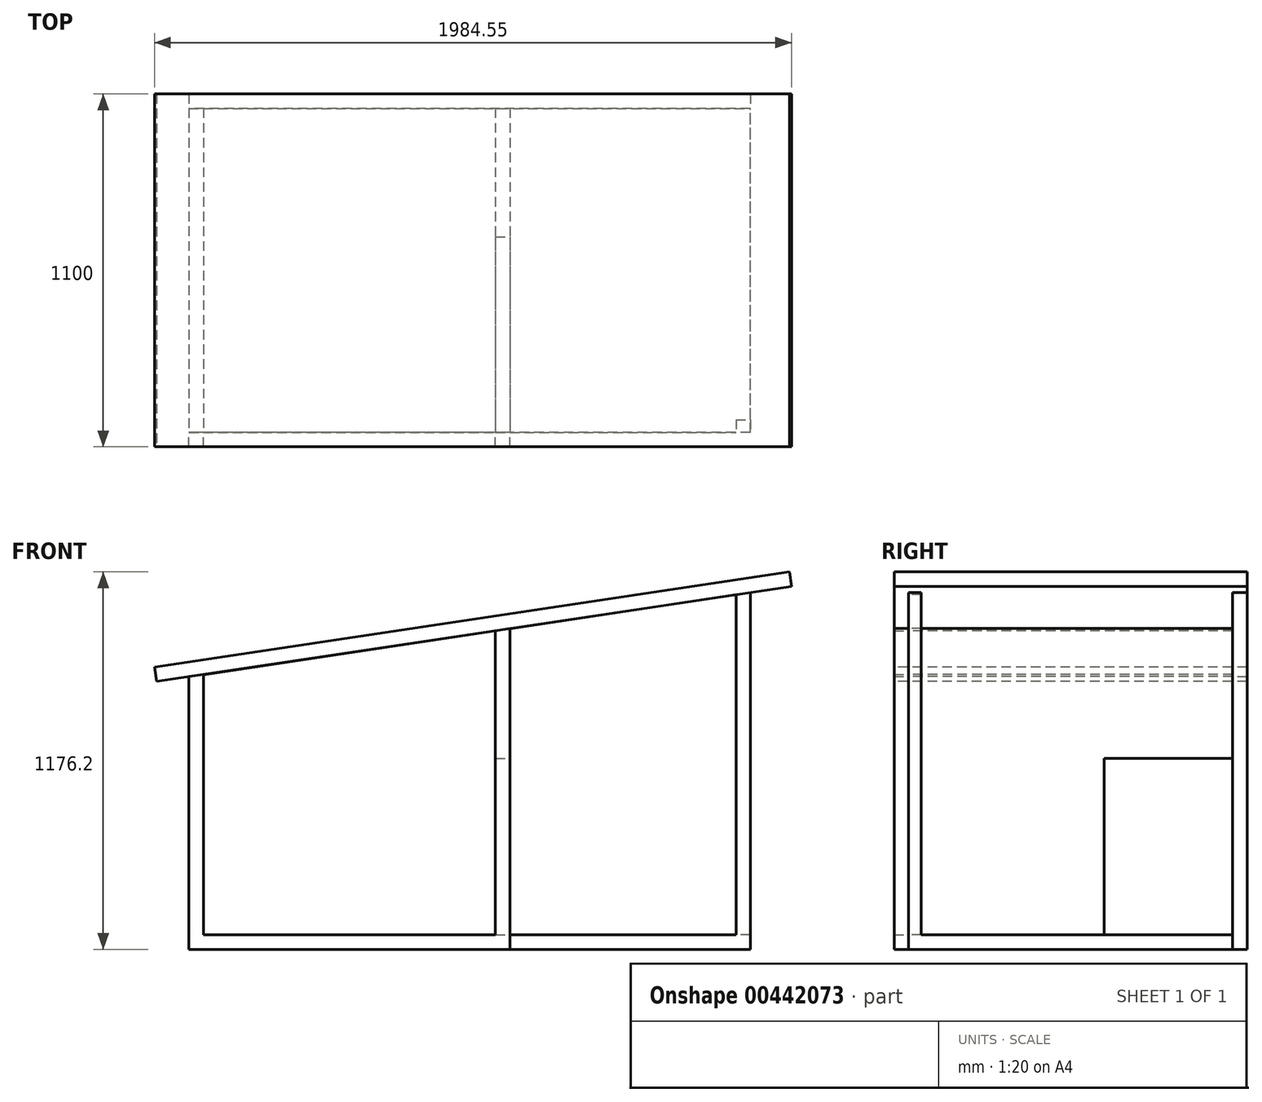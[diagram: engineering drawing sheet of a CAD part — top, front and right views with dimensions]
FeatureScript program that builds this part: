
annotation { "Feature Type Name" : "Feature", "Feature Type Description" : "" }
export const myFeature = defineFeature(function(context is Context, id is Id, definition is map)
    precondition{}
    {
        {
            var Q0;
            Q0=qCreatedBy(makeId("Front.planeOp"),FACE);
            var sketch = newSketch(context, id + "F0", { "sketchPlane" : qUnion([Q0])});
            skLineSegment(sketch, "E0", {"start": v(0, 1000) * mm, "end": v(0, 0) * mm});
            skLineSegment(sketch, "E1", {"start": v(0, 0) * mm, "end": v(-1000, 0) * mm});
            skLineSegment(sketch, "E2", {"start": v(-1000, 0) * mm, "end": v(-1000, 850) * mm});
            skLineSegment(sketch, "E3", {"start": v(-1100, 835) * mm, "end": v(877.87, 1131.68) * mm});
            skLineSegment(sketch, "E4", {"start": v(-1100, 835) * mm, "end": v(-1000, 835) * mm, "construction": true});
            skLineSegment(sketch, "E5", {"start": v(-1100, 835) * mm, "end": v(-1106.68, 879.5) * mm});
            skLineSegment(sketch, "E6", {"start": v(-1106.68, 879.5) * mm, "end": v(871.3, 1176.2) * mm});
            skLineSegment(sketch, "E7", {"start": v(871.3, 1176.2) * mm, "end": v(877.87, 1131.68) * mm});
            skLineSegment(sketch, "E8", {"start": v(-955, 856.75) * mm, "end": v(-955, 0) * mm});
            skLineSegment(sketch, "E9", {"start": v(-45, 993.25) * mm, "end": v(-45, 0) * mm});
            skLineSegment(sketch, "E10", {"start": v(0, 0) * mm, "end": v(750, 0) * mm, "construction": true});
            skLineSegment(sketch, "E11", {"start": v(750, 0) * mm, "end": v(750, 1112.5) * mm, "construction": true});
            skLineSegment(sketch, "E12", {"start": v(877.87, 1131.68) * mm, "end": v(877.87, 1112.5) * mm, "construction": true});
            skLineSegment(sketch, "E13", {"start": v(750, 1112.5) * mm, "end": v(877.87, 1112.5) * mm, "construction": true});
            skLineSegment(sketch, "E14.bottom", {"start": v(-45, 0) * mm, "end": v(0, 0) * mm});
            skLineSegment(sketch, "E14.top", {"start": v(-45, 45) * mm, "end": v(0, 45) * mm});
            skLineSegment(sketch, "E14.left", {"start": v(-45, 0) * mm, "end": v(-45, 45) * mm});
            skLineSegment(sketch, "E14.right", {"start": v(0, 0) * mm, "end": v(0, 45) * mm});
            skSolve(sketch);
        }
        {
            var Q0;
            {var subQ0=sQuery(id+"F0.wireOp",EDGE,"E2");Q0=makeQuery(id+"F0.imprint","IMPRINT",FACE,{"disambiguationData":[TD([[makeQuery(id+"F0.imprint","IMPRINT",EDGE,{"derivedFrom":subQ0}),-1.0]])]});}
            var Q1;
            {var subQ0=sQuery(id+"F0.wireOp",EDGE,"E0");Q1=makeQuery(id+"F0.imprint","IMPRINT",FACE,{"disambiguationData":[TD([[makeQuery(id+"F0.imprint","IMPRINT",EDGE,{"derivedFrom":subQ0}),-1.0]])]});}
            extrude(context, id + "F1", {"entities" : qUnion([Q0, Q1]), "oppositeDirection" : true, "depth" : 1010 * mm});
        }
        {
            var Q0;
            {var subQ5=sQuery(id+"F0.wireOp",EDGE,"E5");Q0=makeQuery(id+"F0.imprint","IMPRINT",FACE,{"disambiguationData":[TD([[makeQuery(id+"F0.imprint","IMPRINT",EDGE,{"derivedFrom":subQ5}),-1.0]])]});}
            extrude(context, id + "F2", {"entities" : qUnion([Q0]), "oppositeDirection" : true, "depth" : 1055 * mm});
        }
        {
            var Q0;
            {var subQ5=sQuery(id+"F0.wireOp",EDGE,"E5");Q0=makeQuery(id+"F0.imprint","IMPRINT",FACE,{"disambiguationData":[TD([[makeQuery(id+"F0.imprint","IMPRINT",EDGE,{"derivedFrom":subQ5}),-1.0]])]});}
            extrude(context, id + "F3", {"entities" : qUnion([Q0]), "operationType" : NewBodyOperationType.ADD, "depth" : 45 * mm});
        }
        {
            var Q0;
            Q0=makeQuery(id+"F1.opExtrude","CAP_FACE",FACE,{"disambiguationData":[OSD([sQuery(id+"F0.wireOp",EDGE,"E0"),sQuery(id+"F0.wireOp",EDGE,"E1"),sQuery(id+"F0.wireOp",EDGE,"E3"),sQuery(id+"F0.wireOp",EDGE,"E9")])],"isStart":false});
            var sketch = newSketch(context, id + "F4", { "sketchPlane" : qUnion([Q0])});
            skLineSegment(sketch, "E15", {"start": v(-750, 0) * mm, "end": v(1000, 0) * mm});
            skLineSegment(sketch, "E16", {"start": v(-750, 0) * mm, "end": v(-750, 1112.5) * mm});
            skLineSegment(sketch, "E17", {"start": v(-750, 1112.5) * mm, "end": v(1000, 849.13) * mm});
            skLineSegment(sketch, "E18", {"start": v(-750, 1112.5) * mm, "end": v(1000, 849.13) * mm, "construction": true});
            skLineSegment(sketch, "E19", {"start": v(1000, 849.13) * mm, "end": v(1000, 0) * mm});
            skSolve(sketch);
        }
        {
            var Q0;
            Q0 = qSketchRegion(id + "F4", true);
            extrude(context, id + "F5", {"entities" : qUnion([Q0]), "depth" : 45 * mm});
        }
        {
            var Q0;
            Q0=makeQuery(id+"F1.opExtrude","SWEPT_FACE",FACE,{"disambiguationData":[OSD([sQuery(id+"F0.wireOp",EDGE,"E0")])]});
            var sketch = newSketch(context, id + "F6", { "sketchPlane" : qUnion([Q0])});
            skLineSegment(sketch, "E20.bottom", {"start": v(1010, 45) * mm, "end": v(610, 45) * mm});
            skLineSegment(sketch, "E20.top", {"start": v(1010, 595) * mm, "end": v(610, 595) * mm});
            skLineSegment(sketch, "E20.left", {"start": v(1010, 45) * mm, "end": v(1010, 595) * mm});
            skLineSegment(sketch, "E20.right", {"start": v(610, 45) * mm, "end": v(610, 595) * mm});
            skSolve(sketch);
        }
        {
            var Q0;
            Q0=makeQuery(id+"F6.imprint","IMPRINT",FACE,{"disambiguationData":[TD([[makeQuery(id+"F6.imprint","IMPRINT",EDGE,{"derivedFrom":sQuery(id+"F6.wireOp",EDGE,"E20.bottom")}),-1.0]])]});
            extrude(context, id + "F7", {"entities" : qUnion([Q0]), "operationType" : NewBodyOperationType.REMOVE, "endBound" : BoundingType.UP_TO_NEXT, "oppositeDirection" : true, "depth" : 25 * mm});
        }
        {
            var Q0;
            {var subQ0=sQuery(id+"F0.wireOp",EDGE,"E1");Q0=makeQuery(id+"F1.opExtrude","SWEPT_FACE",FACE,{"disambiguationData":[OSD([subQ0]),TDD([makeQuery(id+"F0.imprint","IMPRINT",EDGE,{"disambiguationData":[TD([[makeQuery(id+"F0.imprint","INTERSECT",VERTEX,{"derivedFrom":[subQ0,sQuery(id+"F0.wireOp",EDGE,"E2")]}),1.0]])],"derivedFrom":subQ0})])]});}
            var sketch = newSketch(context, id + "F8", { "sketchPlane" : qUnion([Q0])});
            skLineSegment(sketch, "E21.bottom", {"start": v(-955, 0) * mm, "end": v(750, 0) * mm});
            skLineSegment(sketch, "E21.top", {"start": v(-955, -1010) * mm, "end": v(750, -1010) * mm});
            skLineSegment(sketch, "E21.left", {"start": v(-955, 90) * mm, "end": v(-955, -1010) * mm});
            skLineSegment(sketch, "E21.right", {"start": v(750, 0) * mm, "end": v(750, -1010) * mm});
            skSolve(sketch);
        }
        {
            var Q0;
            Q0=makeQuery(id+"F8.imprint","IMPRINT",FACE,{"disambiguationData":[TD([[makeQuery(id+"F8.imprint","IMPRINT",EDGE,{"derivedFrom":sQuery(id+"F8.wireOp",EDGE,"E21.bottom")}),-1.0]])]});
            extrude(context, id + "F9", {"entities" : qUnion([Q0]), "oppositeDirection" : true, "depth" : 45 * mm});
        }
        {
            var Q0;
            Q0=makeQuery(id+"F9.opExtrude","CAP_FACE",FACE,{"disambiguationData":[OSD([sQuery(id+"F8.wireOp",EDGE,"E21.bottom"),sQuery(id+"F8.wireOp",EDGE,"E21.top"),sQuery(id+"F8.wireOp",EDGE,"E21.left"),sQuery(id+"F8.wireOp",EDGE,"E21.right")])],"isStart":false});
            var sketch = newSketch(context, id + "F10", { "sketchPlane" : qUnion([Q0])});
            skLineSegment(sketch, "E22", {"start": v(0, 0) * mm, "end": v(750, 0) * mm, "construction": true});
            skLineSegment(sketch, "E23", {"start": v(750, 1010) * mm, "end": v(750, 0) * mm, "construction": true});
            skLineSegment(sketch, "E24.bottom", {"start": v(750, 0) * mm, "end": v(705, 0) * mm});
            skLineSegment(sketch, "E24.top", {"start": v(750, 39.5) * mm, "end": v(705, 39.5) * mm});
            skLineSegment(sketch, "E24.left", {"start": v(750, 0) * mm, "end": v(750, 39.5) * mm});
            skLineSegment(sketch, "E24.right", {"start": v(705, 0) * mm, "end": v(705, 39.5) * mm});
            skSolve(sketch);
        }
        {
            var Q0;
            Q0 = qSketchRegion(id + "F10", true);
            extrude(context, id + "F11", {"entities" : qUnion([Q0]), "operationType" : NewBodyOperationType.ADD, "endBound" : BoundingType.UP_TO_NEXT, "depth" : 25 * mm});
        }
        {
            var Q0;
            Q0=makeQuery(id+"F1.opExtrude","CAP_FACE",FACE,{"disambiguationData":[OSD([sQuery(id+"F0.wireOp",EDGE,"E1"),sQuery(id+"F0.wireOp",EDGE,"E2"),sQuery(id+"F0.wireOp",EDGE,"E3"),sQuery(id+"F0.wireOp",EDGE,"E8")])],"isStart":true});
            var sketch = newSketch(context, id + "F12", { "sketchPlane" : qUnion([Q0])});
            skLineSegment(sketch, "E25", {"start": v(-1000, 850) * mm, "end": v(0, 1000) * mm});
            skLineSegment(sketch, "E26", {"start": v(0, 1000) * mm, "end": v(0, 0) * mm});
            skLineSegment(sketch, "E27", {"start": v(0, 0) * mm, "end": v(-1000, 0) * mm});
            skLineSegment(sketch, "E28", {"start": v(-1000, 0) * mm, "end": v(-1000, 850) * mm});
            skSolve(sketch);
        }
        {
            var Q0;
            {var subQ2=sQuery(id+"F12.wireOp",EDGE,"E26");Q0=makeQuery(id+"F12.imprint","IMPRINT",FACE,{"disambiguationData":[TD([[makeQuery(id+"F12.imprint","IMPRINT",EDGE,{"derivedFrom":subQ2}),-1.0]])]});}
            var Q1;
            {var subQ0=sQuery(id+"F12.wireOp",EDGE,"E28");Q1=makeQuery(id+"F12.imprint","IMPRINT",FACE,{"disambiguationData":[TD([[makeQuery(id+"F12.imprint","IMPRINT",EDGE,{"derivedFrom":subQ0}),-1.0]])]});}
            extrude(context, id + "F13", {"entities" : qUnion([Q0, Q1]), "depth" : 45 * mm});
        }
    });
